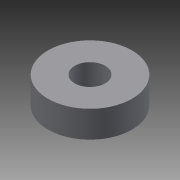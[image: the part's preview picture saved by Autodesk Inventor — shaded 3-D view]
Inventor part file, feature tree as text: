
AUTODESK INVENTOR PART (.ipt)
format: ipt  version: 2013 (Build 170138000, 138)  size: 73,216 bytes
history: native  units: mm
features: extrude x1, sketch x1
ambient origin geometry x8: Origin, YZ Plane, XZ Plane, XY Plane, X Axis, Y Axis, Z Axis, Center Point
bodies: Solid1 (feature_tree)
feature tree (2):
  extrude  "Extrusion1"  Depth=22.0mm
  sketch  "Sketch1"  dims[d0=8.0mm d2=22.0mm d3=7.0mm d4=0.0mm]
